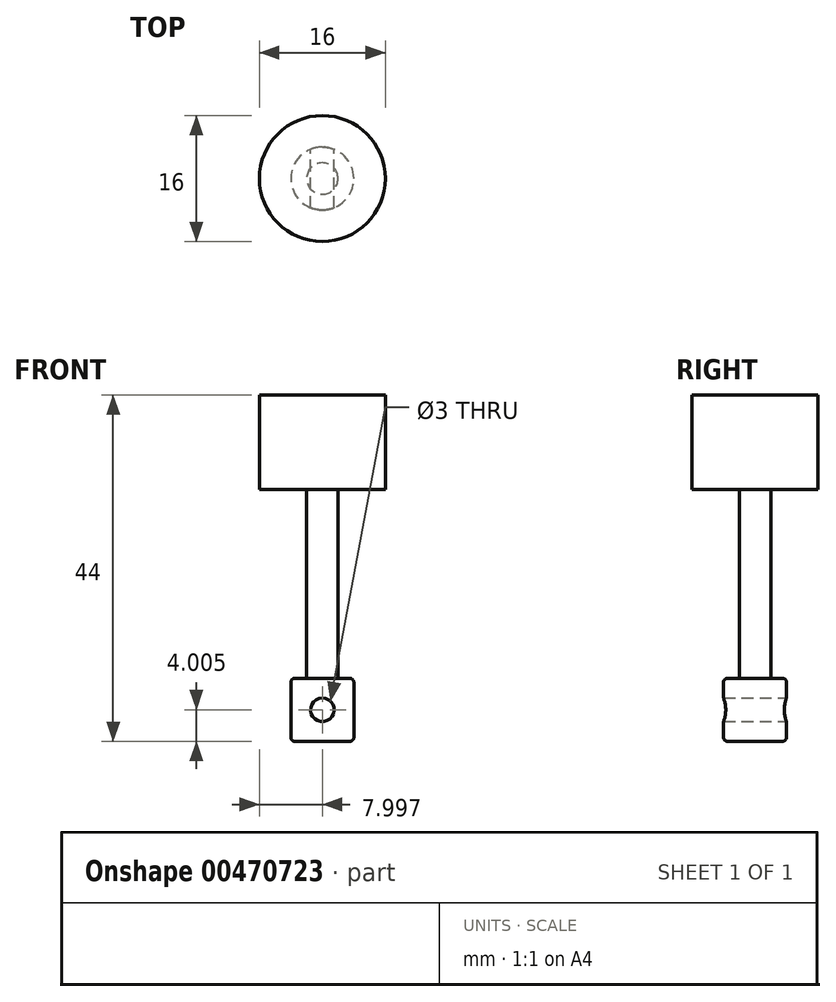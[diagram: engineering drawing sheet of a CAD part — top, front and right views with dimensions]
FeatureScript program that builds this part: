
annotation { "Feature Type Name" : "Feature", "Feature Type Description" : "" }
export const myFeature = defineFeature(function(context is Context, id is Id, definition is map)
    precondition{}
    {
        {
            var Q0;
            Q0=qCreatedBy(makeId("Front.planeOp"),FACE);
            var sketch = newSketch(context, id + "F0", { "sketchPlane" : qUnion([Q0])});
            skLineSegment(sketch, "E0", {"start": v(-23.45, 19.21) * mm, "end": v(-23.45, -24.79) * mm});
            skLineSegment(sketch, "E1", {"start": v(-23.45, -24.79) * mm, "end": v(-26.95, -24.79) * mm});
            skLineSegment(sketch, "E2", {"start": v(-27.45, -24.29) * mm, "end": v(-27.45, -17.29) * mm});
            skLineSegment(sketch, "E3", {"start": v(-26.95, -16.79) * mm, "end": v(-25.45, -16.79) * mm});
            skLineSegment(sketch, "E4", {"start": v(-25.45, -16.79) * mm, "end": v(-25.45, 7.21) * mm});
            skLineSegment(sketch, "E5", {"start": v(-25.45, 7.21) * mm, "end": v(-31.45, 7.21) * mm});
            skLineSegment(sketch, "E6", {"start": v(-31.45, 7.21) * mm, "end": v(-31.45, 19.21) * mm});
            skLineSegment(sketch, "E7", {"start": v(-31.45, 19.21) * mm, "end": v(-23.45, 19.21) * mm});
            skLineSegment(sketch, "E8", {"start": v(-23.45, 19.21) * mm, "end": v(-23.45, -20.79) * mm, "construction": true});
            skPoint(sketch, "E9", {"position": v(-23.45, -20.79) * mm});
            skPoint(sketch, "E10.visualSharp", {"position": v(-27.45, -16.79) * mm});
            skArc(sketch, "E10.filletArc", {"start": v(-26.95, -16.79) * mm, "mid": v(-27.3, -16.93) * mm, "end": v(-27.45, -17.29) * mm});
            skPoint(sketch, "E11.visualSharp", {"position": v(-27.45, -24.79) * mm});
            skArc(sketch, "E11.filletArc", {"start": v(-27.45, -24.29) * mm, "mid": v(-27.3, -24.64) * mm, "end": v(-26.95, -24.79) * mm});
            skSolve(sketch);
        }
        {
            var Q0;
            Q0=makeQuery(id+"F0.imprint","IMPRINT",FACE,{"disambiguationData":[TD([[makeQuery(id+"F0.imprint","IMPRINT",EDGE,{"derivedFrom":sQuery(id+"F0.wireOp",EDGE,"E0")}),-1.0]])]});
            var Q1;
            Q1=sQuery(id+"F0.wireOp",EDGE,"E0");
            revolve(context, id + "F1", {"entities" : qUnion([Q0]), "axis" : qUnion([Q1]), "revolveType" : RevolveType.FULL});
        }
        {
            var Q0;
            Q0=sQuery(id+"F0.wireOp",VERTEX,"E9");
            var Q1;
            Q1=makeQuery(id+"F1.opRevolve","SWEPT_BODY",BODY,{"disambiguationData":[OSD([sQuery(id+"F0.wireOp",EDGE,"E0"),sQuery(id+"F0.wireOp",EDGE,"E1"),sQuery(id+"F0.wireOp",EDGE,"E2"),sQuery(id+"F0.wireOp",EDGE,"E3"),sQuery(id+"F0.wireOp",EDGE,"E4"),sQuery(id+"F0.wireOp",EDGE,"E5"),sQuery(id+"F0.wireOp",EDGE,"E6"),sQuery(id+"F0.wireOp",EDGE,"E7")])]});
            hole(context, id + "F2", {"style" : HoleStyle.SIMPLE, "endStyle" : HoleEndStyle.THROUGH, "oppositeDirection" : true, "holeDiameter" : 3 * mm, "isTappedThrough" : true, "tappedDepth" : 12 * mm, "tapClearance" : 3, "startFromSketch" : true, "locations" : qUnion([Q0]), "scope" : qUnion([Q1])});
        }
        {
            var Q0;
            Q0=sQuery(id+"F0.wireOp",VERTEX,"E9");
            var Q1;
            Q1=makeQuery(id+"F1.opRevolve","SWEPT_BODY",BODY,{"disambiguationData":[OSD([sQuery(id+"F0.wireOp",EDGE,"E0"),sQuery(id+"F0.wireOp",EDGE,"E1"),sQuery(id+"F0.wireOp",EDGE,"E2"),sQuery(id+"F0.wireOp",EDGE,"E3"),sQuery(id+"F0.wireOp",EDGE,"E4"),sQuery(id+"F0.wireOp",EDGE,"E5"),sQuery(id+"F0.wireOp",EDGE,"E6"),sQuery(id+"F0.wireOp",EDGE,"E7")])]});
            hole(context, id + "F3", {"style" : HoleStyle.SIMPLE, "endStyle" : HoleEndStyle.THROUGH, "holeDiameter" : 3 * mm, "isTappedThrough" : true, "tappedDepth" : 12 * mm, "tapClearance" : 3, "startFromSketch" : true, "locations" : qUnion([Q0]), "scope" : qUnion([Q1])});
        }
    });
